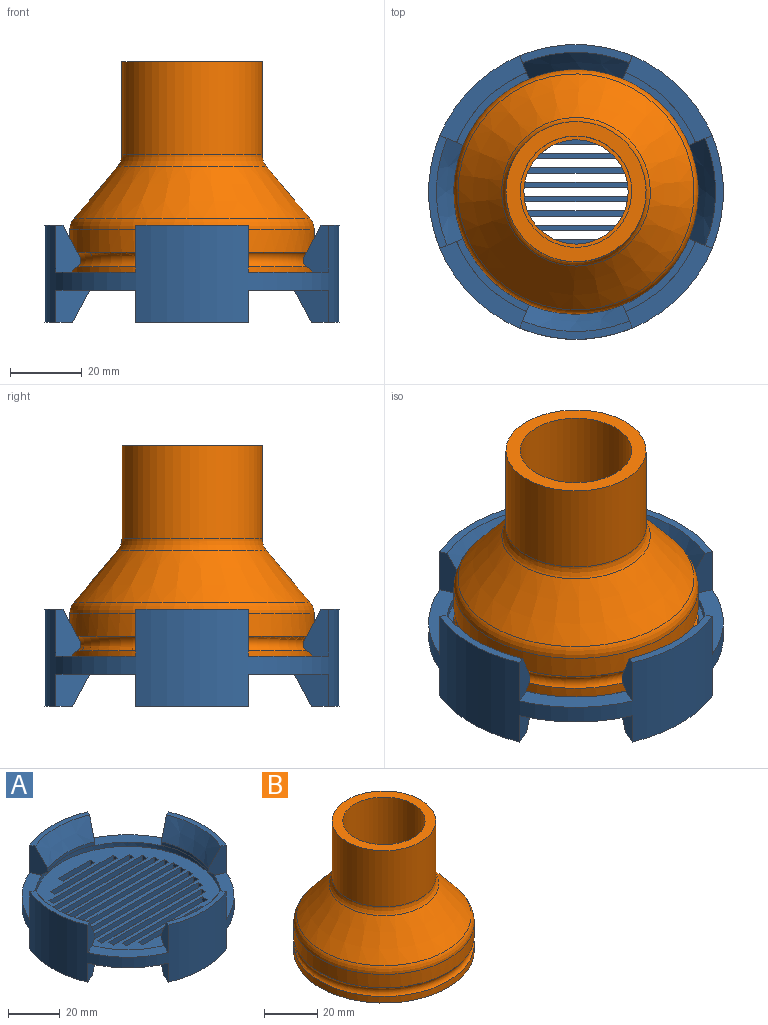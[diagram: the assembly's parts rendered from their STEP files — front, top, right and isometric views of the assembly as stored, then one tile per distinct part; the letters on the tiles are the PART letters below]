
ASSEMBLY  parts=2 mates=1
PART A: 123 faces, bbox 82x82x27 mm
  f0: cylinder r=41mm len=82mm, axis (0,0,-1), area 4121.8mm2, adj f5,f9,f13,f32,f34,f35,f36,f38
  f1: cylinder r=36mm len=72mm, axis (0,0,-1), area 508.9mm2, adj f2,f6,f10,f14,f17,f111,f112,f113
  f2: cone r=33.5mm half-angle=55deg, axis (0,0,-1), area 83.3mm2, adj f1,f3,f112,f120
  f3: cylinder r=33.5mm len=25.64mm, axis (0,0,-1), area 39.5mm2, adj f2,f4,f112,f120
  f4: cone r=38.84mm half-angle=30deg, axis (0,0,1), area 303.4mm2, adj f3,f38,f112,f120
  f5: plane 31.38x5.12mm, normal (0,0,1), area 67.7mm2, adj f0,f8,f117,f121
  f6: cone r=33.5mm half-angle=55deg, axis (0,0,-1), area 83.3mm2, adj f1,f7,f117,f121
  f7: cylinder r=33.5mm len=25.64mm, axis (0,0,-1), area 39.5mm2, adj f6,f8,f117,f121
  f8: cone r=38.84mm half-angle=30deg, axis (0,0,1), area 303.4mm2, adj f5,f7,f117,f121
  f9: plane 31.38x5.12mm, normal (0,0,1), area 67.7mm2, adj f0,f12,f114,f118
  f10: cone r=33.5mm half-angle=55deg, axis (0,0,-1), area 83.3mm2, adj f1,f11,f114,f118
  f11: cylinder r=33.5mm len=25.64mm, axis (0,0,-1), area 39.5mm2, adj f10,f12,f114,f118
  f12: cone r=38.84mm half-angle=30deg, axis (0,0,1), area 303.4mm2, adj f9,f11,f114,f118
  f13: plane 31.38x5.12mm, normal (0,0,1), area 67.7mm2, adj f0,f16,f111,f115
  f14: cone r=33.5mm half-angle=55deg, axis (0,0,-1), area 83.3mm2, adj f1,f15,f111,f115
  f15: cylinder r=33.5mm len=25.64mm, axis (0,0,-1), area 39.5mm2, adj f14,f16,f111,f115
  f16: cone r=38.84mm half-angle=30deg, axis (0,0,1), area 303.4mm2, adj f13,f15,f111,f115
  f17: plane 72x72mm, normal (0,0,1), area 2326.2mm2, adj f1,f51,f52,f53,f54,f55,f56,f57
  f18: plane 43.8x4mm, normal (0,0,-1), area 71.8mm2, adj f33,f99,f100,f102,f108
  f19: plane 17.39x1.27mm, normal (0,0,-1), area 14.7mm2, adj f33,f104
  f20: plane 50.34x4mm, normal (0,0,-1), area 79.5mm2, adj f33,f92,f107,f109,f110
  f21: plane 34.27x4mm, normal (0,0,-1), area 64.3mm2, adj f33,f56,f57,f58,f98
  f22: plane 34.27x4mm, normal (0,0,-1), area 64.3mm2, adj f33,f101,f103,f105,f106
  f23: plane 54.98x4mm, normal (0,0,-1), area 85.3mm2, adj f33,f88,f91,f93,f94
  f24: plane 58.16x4mm, normal (0,0,-1), area 89.3mm2, adj f33,f84,f87,f89,f90
  f25: plane 60.12x4mm, normal (0,0,-1), area 91.5mm2, adj f33,f80,f83,f85,f86
  f26: plane 60.12x4mm, normal (0,0,-1), area 91.5mm2, adj f33,f68,f76,f77,f78
  f27: plane 50.34x4mm, normal (0,0,-1), area 79.5mm2, adj f33,f64,f72,f73,f74
  f28: plane 61.03x10.5mm, normal (0,0,-1), area 187mm2, adj f33,f51,f52,f53,f54,f67,f69,f70
  f29: plane 54.98x4mm, normal (0,0,-1), area 85.3mm2, adj f33,f59,f63,f65,f66
  f30: plane 58.16x4mm, normal (0,0,-1), area 89.3mm2, adj f33,f60,f61,f62,f75
  f31: plane 43.8x4mm, normal (0,0,-1), area 71.8mm2, adj f33,f71,f95,f96,f97
  f32: plane 31.38x7.74mm, normal (0,0,-1), area 151.2mm2, adj f0,f33,f40,f48
  f33: cone r=36mm half-angle=30deg, axis (0,0,-1), area 1201.7mm2, adj f18,f19,f20,f21,f22,f23,f24,f25
  f34: plane 31.38x7.74mm, normal (0,0,-1), area 151.2mm2, adj f0,f33,f45,f49
  f35: plane 31.38x7.74mm, normal (0,0,-1), area 151.2mm2, adj f0,f33,f42,f46
  f36: plane 31.38x7.74mm, normal (0,0,-1), area 151.2mm2, adj f0,f33,f39,f43
  f37: plane 17.39x1.27mm, normal (0,0,-1), area 14.7mm2, adj f33,f55
  f38: plane 31.38x5.12mm, normal (0,0,1), area 67.7mm2, adj f0,f4,f112,f120
  f39: plane 9.42x9mm, normal (0.38,-0.92,0), area 68.4mm2, adj f0,f33,f36,f41
  f40: plane 9.42x9mm, normal (-0.92,0.38,0), area 68.4mm2, adj f0,f32,f33,f41
  f41: plane 26.09x26.09mm, normal (0,0,-1), area 287.5mm2, adj f0,f33,f39,f40
  f42: plane 9.42x9mm, normal (-0.92,-0.38,0), area 68.4mm2, adj f0,f33,f35,f44
  f43: plane 9.42x9mm, normal (0.38,0.92,0), area 68.4mm2, adj f0,f33,f36,f44
  f44: plane 26.09x26.09mm, normal (0,0,-1), area 287.5mm2, adj f0,f33,f42,f43
  f45: plane 9.42x9mm, normal (-0.38,0.92,0), area 68.4mm2, adj f0,f33,f34,f47
  f46: plane 9.42x9mm, normal (0.92,-0.38,0), area 68.4mm2, adj f0,f33,f35,f47
  f47: plane 26.09x26.09mm, normal (0,0,-1), area 287.5mm2, adj f0,f33,f45,f46
  f48: plane 9.42x9mm, normal (0.92,0.38,0), area 68.4mm2, adj f0,f32,f33,f50
  f49: plane 9.42x9mm, normal (-0.38,-0.92,0), area 68.4mm2, adj f0,f33,f34,f50
  f50: plane 26.09x26.09mm, normal (0,0,-1), area 287.5mm2, adj f0,f33,f48,f49
  f51: plane 2.5x2.5mm, normal (-1,0,0), area 6.3mm2, adj f17,f28,f52,f53
  f52: plane 60x2.5mm, normal (0,-1,0), area 150mm2, adj f17,f28,f51,f54
  f53: plane 60x2.5mm, normal (0,1,0), area 150mm2, adj f17,f28,f51,f54
  f54: plane 2.5x2.5mm, normal (1,0,0), area 6.3mm2, adj f17,f28,f52,f53
  f55: plane 17.39x2.5mm, normal (0,1,0), area 43.5mm2, adj f17,f37,f56,f57
  f56: plane 2.5x2.5mm, normal (-1,0,0), area 6.3mm2, adj f17,f21,f55,f58
  f57: plane 2.5x2.5mm, normal (1,0,0), area 6.3mm2, adj f17,f21,f55,f58
  f58: plane 17.39x2.5mm, normal (0,-1,0), area 43.5mm2, adj f17,f21,f56,f57
  f59: plane 54.98x2.5mm, normal (0,1,0), area 137.4mm2, adj f17,f29,f60,f61
  f60: plane 2.5x2.5mm, normal (-1,0,0), area 6.3mm2, adj f17,f30,f59,f62
  f61: plane 2.5x2.5mm, normal (1,0,0), area 6.3mm2, adj f17,f30,f59,f62
  f62: plane 54.98x2.5mm, normal (0,-1,0), area 137.4mm2, adj f17,f30,f60,f61
  f63: plane 2.5x2.5mm, normal (-1,0,0), area 6.3mm2, adj f17,f29,f64,f65
  f64: plane 50.34x2.5mm, normal (0,1,0), area 125.9mm2, adj f17,f27,f63,f66
  f65: plane 50.34x2.5mm, normal (0,-1,0), area 125.9mm2, adj f17,f29,f63,f66
  f66: plane 2.5x2.5mm, normal (1,0,0), area 6.3mm2, adj f17,f29,f64,f65
  f67: plane 2.5x2.5mm, normal (1,0,0), area 6.3mm2, adj f17,f28,f68,f69
  f68: plane 60.12x2.5mm, normal (0,1,0), area 150.3mm2, adj f17,f26,f67,f70
  f69: plane 60.12x2.5mm, normal (0,-1,0), area 150.3mm2, adj f17,f28,f67,f70
  f70: plane 2.5x2.5mm, normal (-1,0,0), area 6.3mm2, adj f17,f28,f68,f69
  f71: plane 43.8x2.5mm, normal (0,1,0), area 109.5mm2, adj f17,f31,f72,f73
  f72: plane 2.5x2.5mm, normal (-1,0,0), area 6.3mm2, adj f17,f27,f71,f74
  f73: plane 2.5x2.5mm, normal (1,0,0), area 6.3mm2, adj f17,f27,f71,f74
  f74: plane 43.8x2.5mm, normal (0,-1,0), area 109.5mm2, adj f17,f27,f72,f73
  f75: plane 58.16x2.5mm, normal (0,1,0), area 145.4mm2, adj f17,f30,f76,f77
  f76: plane 2.5x2.5mm, normal (-1,0,0), area 6.3mm2, adj f17,f26,f75,f78
  f77: plane 2.5x2.5mm, normal (1,0,0), area 6.3mm2, adj f17,f26,f75,f78
  f78: plane 58.16x2.5mm, normal (0,-1,0), area 145.4mm2, adj f17,f26,f76,f77
  f79: plane 2.5x2.5mm, normal (-1,0,0), area 6.3mm2, adj f17,f28,f80,f81
  f80: plane 60.12x2.5mm, normal (0,-1,0), area 150.3mm2, adj f17,f25,f79,f82
  f81: plane 60.12x2.5mm, normal (0,1,0), area 150.3mm2, adj f17,f28,f79,f82
  f82: plane 2.5x2.5mm, normal (1,0,0), area 6.3mm2, adj f17,f28,f80,f81
  f83: plane 2.5x2.5mm, normal (-1,0,0), area 6.3mm2, adj f17,f25,f84,f85
  f84: plane 58.16x2.5mm, normal (0,-1,0), area 145.4mm2, adj f17,f24,f83,f86
  f85: plane 58.16x2.5mm, normal (0,1,0), area 145.4mm2, adj f17,f25,f83,f86
  f86: plane 2.5x2.5mm, normal (1,0,0), area 6.3mm2, adj f17,f25,f84,f85
  f87: plane 2.5x2.5mm, normal (-1,0,0), area 6.3mm2, adj f17,f24,f88,f89
  f88: plane 54.98x2.5mm, normal (0,-1,0), area 137.4mm2, adj f17,f23,f87,f90
  f89: plane 54.98x2.5mm, normal (0,1,0), area 137.4mm2, adj f17,f24,f87,f90
  f90: plane 2.5x2.5mm, normal (1,0,0), area 6.3mm2, adj f17,f24,f88,f89
  f91: plane 2.5x2.5mm, normal (-1,0,0), area 6.3mm2, adj f17,f23,f92,f93
  f92: plane 50.34x2.5mm, normal (0,-1,0), area 125.9mm2, adj f17,f20,f91,f94
  f93: plane 50.34x2.5mm, normal (0,1,0), area 125.9mm2, adj f17,f23,f91,f94
  f94: plane 2.5x2.5mm, normal (1,0,0), area 6.3mm2, adj f17,f23,f92,f93
  f95: plane 34.27x2.5mm, normal (0,-1,0), area 85.7mm2, adj f17,f31,f96,f97
  f96: plane 2.5x2.5mm, normal (1,0,0), area 6.3mm2, adj f17,f31,f95,f98
  f97: plane 2.5x2.5mm, normal (-1,0,0), area 6.3mm2, adj f17,f31,f95,f98
  f98: plane 34.27x2.5mm, normal (0,1,0), area 85.7mm2, adj f17,f21,f96,f97
  f99: plane 2.5x2.5mm, normal (1,0,0), area 6.3mm2, adj f17,f18,f100,f101
  f100: plane 34.27x2.5mm, normal (0,1,0), area 85.7mm2, adj f17,f18,f99,f102
  f101: plane 34.27x2.5mm, normal (0,-1,0), area 85.7mm2, adj f17,f22,f99,f102
  f102: plane 2.5x2.5mm, normal (-1,0,0), area 6.3mm2, adj f17,f18,f100,f101
  f103: plane 2.5x2.5mm, normal (-1,0,0), area 6.3mm2, adj f17,f22,f104,f105
  f104: plane 17.39x2.5mm, normal (0,-1,0), area 43.5mm2, adj f17,f19,f103,f106
  f105: plane 17.39x2.5mm, normal (0,1,0), area 43.5mm2, adj f17,f22,f103,f106
  f106: plane 2.5x2.5mm, normal (1,0,0), area 6.3mm2, adj f17,f22,f104,f105
  f107: plane 2.5x2.5mm, normal (-1,0,0), area 6.3mm2, adj f17,f20,f108,f109
  f108: plane 43.8x2.5mm, normal (0,-1,0), area 109.5mm2, adj f17,f18,f107,f110
  f109: plane 43.8x2.5mm, normal (0,1,0), area 109.5mm2, adj f17,f20,f107,f110
  f110: plane 2.5x2.5mm, normal (1,0,0), area 6.3mm2, adj f17,f20,f108,f109
  f111: plane 13x6.93mm, normal (-0.38,-0.92,0), area 69.4mm2, adj f0,f1,f13,f14,f15,f16,f113
  f112: plane 13x6.93mm, normal (0.92,0.38,0), area 69.4mm2, adj f0,f1,f2,f3,f4,f38,f113
  f113: plane 24.1x24.1mm, normal (0,0,1), area 151.2mm2, adj f0,f1,f111,f112
  f114: plane 13x6.93mm, normal (0.92,-0.38,0), area 69.4mm2, adj f0,f1,f9,f10,f11,f12,f116
  f115: plane 13x6.93mm, normal (-0.38,0.92,0), area 69.4mm2, adj f0,f1,f13,f14,f15,f16,f116
  f116: plane 24.1x24.1mm, normal (0,0,1), area 151.2mm2, adj f0,f1,f114,f115
  f117: plane 13x6.93mm, normal (0.38,0.92,0), area 69.4mm2, adj f0,f1,f5,f6,f7,f8,f119
  f118: plane 13x6.93mm, normal (-0.92,-0.38,0), area 69.4mm2, adj f0,f1,f9,f10,f11,f12,f119
  f119: plane 24.1x24.1mm, normal (0,0,1), area 151.2mm2, adj f0,f1,f117,f118
  f120: plane 13x6.93mm, normal (-0.92,0.38,0), area 69.4mm2, adj f0,f1,f2,f3,f4,f38,f122
  f121: plane 13x6.93mm, normal (0.38,-0.92,0), area 69.4mm2, adj f0,f1,f5,f6,f7,f8,f122
  f122: plane 24.1x24.1mm, normal (0,0,1), area 151.2mm2, adj f0,f1,f120,f121
PART B: 33 faces, bbox 76.9x76.9x60 mm
  f0: cylinder r=34mm len=68mm, axis (0,0,-1), area 1320.3mm2, adj f29,f31
  f1: cylinder r=34mm len=68mm, axis (0,0,-1), area 640.9mm2, adj f19,f29
  f2: plane 26.38x2.31mm, normal (-0.38,-0.92,0), area 62.2mm2, adj f3,f5,f18,f25
  f3: cylinder r=18.5mm len=23.4mm, axis (0,0,-1), area 339.9mm2, adj f2,f4,f18,f25
  f4: plane 26.38x2.31mm, normal (0.92,0.38,0), area 62.2mm2, adj f3,f5,f18,f25
  f5: cylinder r=16mm len=26.38mm, axis (0,0,-1), area 331.4mm2, adj f2,f4,f18,f25
  f6: plane 26.38x2.31mm, normal (-0.92,0.38,0), area 62.2mm2, adj f7,f9,f18,f25
  f7: cylinder r=18.5mm len=23.4mm, axis (0,0,-1), area 339.9mm2, adj f6,f8,f18,f25
  f8: plane 26.38x2.31mm, normal (0.38,-0.92,0), area 62.2mm2, adj f7,f9,f18,f25
  f9: cylinder r=16mm len=26.38mm, axis (0,0,-1), area 331.4mm2, adj f6,f8,f18,f25
  f10: cylinder r=16mm len=26.38mm, axis (0,0,-1), area 331.4mm2, adj f11,f13,f18,f25
  f11: plane 26.38x2.31mm, normal (0.38,0.92,0), area 62.2mm2, adj f10,f12,f18,f25
  f12: cylinder r=18.5mm len=23.4mm, axis (0,0,-1), area 339.9mm2, adj f11,f13,f18,f25
  f13: plane 26.38x2.31mm, normal (-0.92,-0.38,0), area 62.2mm2, adj f10,f12,f18,f25
  f14: plane 26.38x2.31mm, normal (-0.38,0.92,0), area 62.2mm2, adj f15,f17,f18,f25
  f15: cylinder r=16mm len=26.38mm, axis (0,0,-1), area 331.4mm2, adj f14,f16,f18,f25
  f16: plane 26.38x2.31mm, normal (0.92,-0.38,0), area 62.2mm2, adj f15,f17,f18,f25
  f17: cylinder r=18.5mm len=23.4mm, axis (0,0,-1), area 339.9mm2, adj f14,f16,f18,f25
  f18: cone r=30mm half-angle=40deg, axis (0,0,-1), area 2354.4mm2, adj f2,f3,f4,f5,f6,f7,f8,f9
  f19: plane 68x68mm, normal (0,0,-1), area 804.2mm2, adj f1,f20
  f20: cylinder r=30mm len=60mm, axis (0,0,-1), area 1706.1mm2, adj f19,f30
  f21: cylinder r=15.5mm len=31mm, axis (0,0,-1), area 2924.5mm2, adj f18,f22
  f22: plane 39x39mm, normal (0,0,1), area 439.8mm2, adj f21,f23
  f23: cylinder r=19.5mm len=39mm, axis (0,0,-1), area 3173.3mm2, adj f22,f32
  f24: cone r=19.5mm half-angle=40deg, axis (0,0,-1), area 3179.7mm2, adj f31,f32
  f25: plane 39x39mm, normal (0,0,1), area 398.6mm2, adj f2,f3,f4,f5,f6,f7,f8,f9
  f26: cylinder r=14.5mm len=29mm, axis (0,0,-1), area 273.3mm2, adj f25,f28
  f27: cylinder r=19.5mm len=39mm, axis (0,0,-1), area 367.6mm2, adj f25,f28
  f28: plane 39x39mm, normal (0,0,-1), area 534.1mm2, adj f26,f27
  f29: torus R=35.5mm, axis (0,0,1), area 971.3mm2, adj f0,f1
  f30: torus R=20mm, axis (0,0,-1), area 1281.2mm2, adj f18,f20
  f31: torus R=29mm, axis (0,0,1), area 737mm2, adj f0,f24
  f32: torus R=24.5mm, axis (0,0,-1), area 436.4mm2, adj f23,f24
PLACE A at identity fixed
PLACE B rot(axis=(0,0,1),5.5deg) t=(0,0,12.54)mm
MATE cylindrical B.f0 <-> A.f0  axis (0,0,-1) through (0,0,14.04)mm
